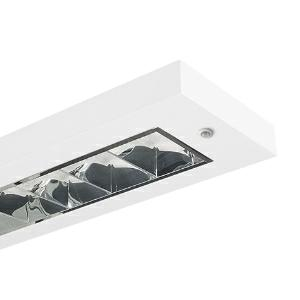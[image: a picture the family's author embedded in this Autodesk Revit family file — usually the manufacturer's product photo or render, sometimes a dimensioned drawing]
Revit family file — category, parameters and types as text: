
# Revit family: 3f_filippi_-_3f_travetta_di_dali_sensor_2mg_3f_filippi_-_11523_-_3f_trav__led_di_2x22w_dali_ls_2mg_l1590_8988
name_source: partatom
category: Lighting Fixtures
units: mm (PartAtom-declared; Revit-internal decimal feet)

## family parameters
Cut with Voids When Loaded = No
Host = Face
Light Source = No
Part Type = Normal
Room Calculation Point = No
Round Connector Dimension = Use Diameter
Shared = No

## types (1)
- 3F Filippi - 3F Travetta DI DALI Sensor 2MG (1 x LED, 5865 lm, 49 W, 4000 K)
    Apparent Load = 49 VA
    Approval mark = ENEC
    CIE Flux Codes = 61 98 100 85 100
    Color Rendering = 80
    Color Temperature = 4000 K
    Control Gear = Electronic transformer
    Default Elevation = 1800 mm
    Description = ILLUMINOTECHNICAL
Luminous efficiency 100% (DLOR 85%, ULOR 15%).
Initial luminous flux of the luminaire 5865 lm.
Symmetric direct-indirect distribution.
Installation Interdistance Transv.D = 2.02 x hu - Long.D = 1.27 x hu.
Average luminance <1000 cd/m² for radial angles >65°.
Tabular UGR (CIE 117 - 4H-8H; S=0.25H; 70/50/20): RUG 18.4 - 17.8.
Beam angle: 99° - 72°.
Luminous efficacy 120 lm/W.
Lifetime (L93/B10): 30000 h. (tq+25°C)
Lifetime (L90/B10): 50000 h. (tq+25°C)
Lifetime (L85/B10): 80000 h. (tq+25°C)
Lifetime (L80/B10): 100000 h. (tq+25°C)
Sudden decreased luminous flux after 50000 hours: 0% (C0).
Photobiological safety in compliance with IEC/TR 62778: RG0 risk exempt, (IEC 62471).
In compliance with IEC/EN 62722-2-1 - IEC/EN 62717 standards.

SOURCE
2 linear LED modules 22W/840.
Energy efficiency class (UE 2019/2020 - UE 2019/2015): D.
CIE 13.3 Colour rendering index: CRI >80 (R9 <50%).
IES TM-30 Fidelity Index: Rf = 84 Rg = 95.
CCT nominal colour temperature 4000 K.
Colour initial tolerance (MacAdam): SDCM 2.

MECHANICAL
Housing with squared shape in white painted galvannealed steel, with nonreflecting surface.
2MG parabolic louvre, high efficiency, in specular aluminium with superficial titanium-magnesium treatment, non-iridescent, with transverse blades closed at the top.
Prismatic flat diffuser in transparent methacrylate (PMMA), multilenticular, anti-glare, prismatic exterior, placed above louvre blades.
Film protective against dust and finger marks, adhesive, attached to louvre.
Upper holes closing film made of opal polycarbonate.
Luminaire with limited surface temperature. - D - (EN 60598-2-24)
Dimensions: 1590x190 mm, height 60 mm (edge 40 mm). Weight 5 kg.
IP20 protection degree.
Mechanical strength to impacts IK02 (0.2 joule).
Glow-wire test resistance 650°C.

ELECTRICAL
Halogen Free DALI electronic wiring 230V-50/60Hz, power factor 0.90 at full load, THD <25%, constant output current, SELV, class I, 1 driver, 1 DALI addresse.
DALI light and presence sensor integrated in the luminarie.
Power of the luminaire 49 W.
CE - IEC 60598-1 - EN 60598-1.
SAFE FLICKER: PstLM=<1 and SVM=<0.4 (IEC TR 61547-1 and IEC TR 63158), to ensure a more comfortable and safe light.
Ambient temperature from 0°C to +25°C.
Temperature class T6 max 85°C.
Relative humidity UR: <85%.

INSTALLATION
Suspended.
All accessories dedicated to this product are available on the Catalog and on our website www.3F-Filippi.com.

APPLICATIONS
In environments, even with reduced height, requiring a comfortable light.
In environments with VDTs, managerial offices and staterooms, public offices and schools.

LIGHT MANAGEMENT
The DALI presence and brightness sensor, integrated in the luminaire, allows you to keep the level of illumination constant as a function of natural light (in addition to switching on/off as a result of presence detection and set twilight threshold).
Recommended installation height up to 10 m.
Commissioning of the control system via free APP; the intervention of a specialist technician can be quoted on request.

WARNING
The luminaire cannot be controlled manually with PUSH-DIM technology.
Luminaire designed for disposal/recycling at end-of-life.
Replaceable (LED only) light source by a professional. Replaceable control gear by a professional.
    Height = 60 mm
    Lamp = 1 x LED
    Lamp Light Flux = 5865 lm
    Lamp Power = 49 W
    Lamp count = 1
    Length = 1590 mm
    Lifetime = 50000 h
    Luminous efficacy = 120 lm/W
    Manufacturer = 3F Filippi
    ModVariant = No
    Model = 3F Filippi - 11523 - 3F Trav. LED DI 2x22W DALI LS 2MG L1590
    Mounting Place = Ceiling
    Mounting Type = Pendant
    Number of Poles = 1
    OnlyDefault = Yes
    Power Factor = 1
    Product Name = 3F Filippi - 3F Travetta DI DALI Sensor 2MG
    Product group = pendant luminaire
    ProductGroupID = 9
    Protection Class = Protection class I
    Protection Degree = IP 20
    RLX_Detail_Level = 1
    RLX_Emergency_Light_Flux = 0 lm
    RLX_Emergency_Type = 0
    RLX_Emergency_Type_DB = No
    RlxData = <blob elided: 52925 chars, md5=8037d209>
    Socket = socket
    Standby Power = 0 W
    System Light Flux = 5865 lm
    System Power = 49 W
    Type Comments = Product without accessories
    Type Image = 3ffilippi_3f_travetta_led_sensor_2mg.jpg
    URL = http://relux.com
    VarID = ---
    Voltage = 0 V
    Weight = 0.00 kg
    Width = 190 mm

## geometry (parser evidence)
native form markers: Blend x4, Sweep x11
no freeform markers — native parametric forms only
